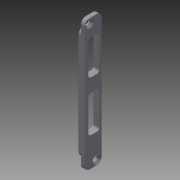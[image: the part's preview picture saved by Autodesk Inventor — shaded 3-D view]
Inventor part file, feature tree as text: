
AUTODESK INVENTOR PART (.ipt)
format: ipt  version: 2013 (Build 170138000, 138)  size: 160,768 bytes
history: native  units: in
note: dims shown in document units (in); Inventor stores cm internally (conversion verified against a paired STEP export)
features: extrude x3, sketch x3, chamfer x1
ambient origin geometry x8: Origin, YZ Plane, XZ Plane, XY Plane, X Axis, Y Axis, Z Axis, Center Point
bodies: Solid1 (feature_tree)
feature tree (7):
  extrude  "Extrusion1"  Depth=0.2677in
  chamfer  "Chamfer1"  Distance=0.0591in
  extrude  "Extrusion2"  Depth=0.0394in
  extrude  "Extrusion3"  Depth=0.0591in
  sketch  "Sketch1"  dims[d0=2.0787in d1=0.2677in]
  sketch  "Sketch2"  dims[d2=0.0787in d3=0.0591in d4=0.0in]
  sketch  "Sketch3"  dims[d6=0.0315in d7=0.0787in d8=45.0deg d9=0.0394in d10=0.0591in d11=0.0591in d12=0.0591in d13=0.0in d14=0.2677in d15=1.7638in d16=0.0787in d17=0.0394in d18=0.0in d19=0.0787in d20=0.0039in d21=0.0039in]
